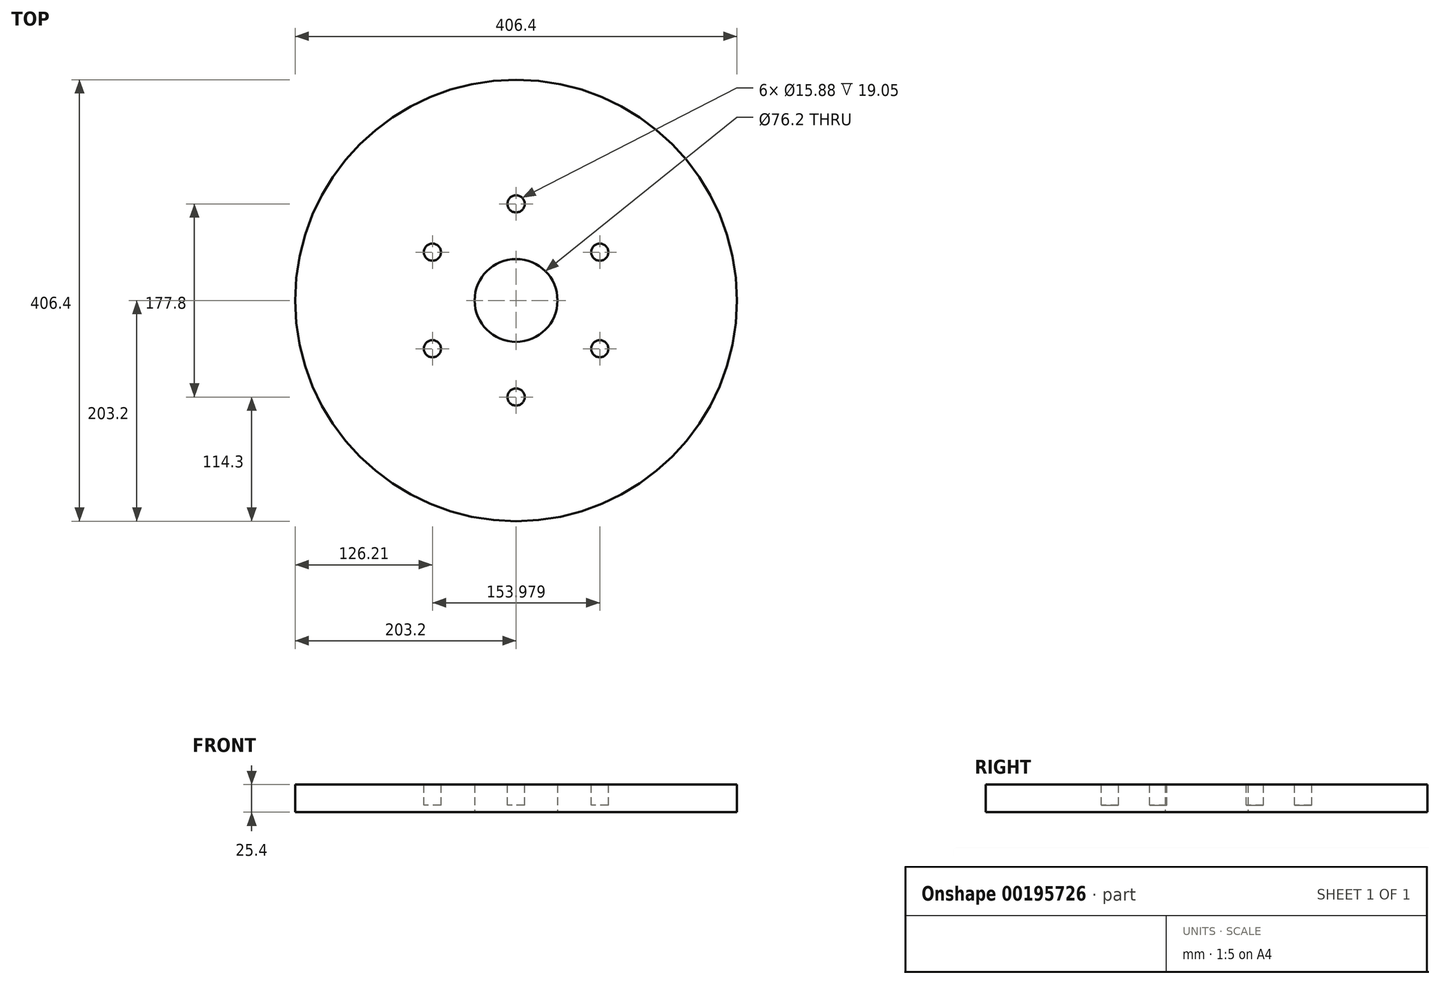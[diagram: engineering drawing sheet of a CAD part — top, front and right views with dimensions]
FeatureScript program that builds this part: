
annotation { "Feature Type Name" : "Feature", "Feature Type Description" : "" }
export const myFeature = defineFeature(function(context is Context, id is Id, definition is map)
    precondition{}
    {
        {
            var Q0;
            Q0=qCreatedBy(makeId("Top.planeOp"),FACE);
            var sketch = newSketch(context, id + "F0", { "sketchPlane" : qUnion([Q0])});
            skCircle(sketch, "E0", {"center": v(0, 0) * mm, "radius": 203.2 * mm});
            skCircle(sketch, "E1", {"center": v(0, 0) * mm, "radius": 38.1 * mm});
            skSolve(sketch);
        }
        {
            var Q0;
            Q0 = qSketchRegion(id + "F0", true);
            extrude(context, id + "F1", {"entities" : qUnion([Q0]), "depth" : 25.4 * mm});
        }
        {
            var Q0;
            Q0=makeQuery(id+"F1.opExtrude","CAP_FACE",FACE,{"disambiguationData":[OSD([sQuery(id+"F0.wireOp",EDGE,"E0"),sQuery(id+"F0.wireOp",EDGE,"E1")])],"isStart":false});
            var sketch = newSketch(context, id + "F2", { "sketchPlane" : qUnion([Q0])});
            skCircle(sketch, "E2", {"center": v(0, 88.9) * mm, "radius": 7.94 * mm});
            skCircle(sketch, "E3.1.0", {"center": v(-76.99, 44.45) * mm, "radius": 7.94 * mm});
            skCircle(sketch, "E3.2.0", {"center": v(-76.99, -44.45) * mm, "radius": 7.94 * mm});
            skCircle(sketch, "E3.3.0", {"center": v(0, -88.9) * mm, "radius": 7.94 * mm});
            skCircle(sketch, "E3.4.0", {"center": v(76.99, -44.45) * mm, "radius": 7.94 * mm});
            skCircle(sketch, "E3.5.0", {"center": v(76.99, 44.45) * mm, "radius": 7.94 * mm});
            skPoint(sketch, "E3.center", {"position": v(0, 0) * mm});
            skLineSegment(sketch, "E4", {"start": v(0, 0) * mm, "end": v(0, 142.6) * mm});
            skLineSegment(sketch, "E5", {"start": v(0, 0) * mm, "end": v(0, 88.9) * mm});
            skSolve(sketch);
        }
        {
            var Q0;
            Q0 = qSketchRegion(id + "F2", true);
            extrude(context, id + "F3", {"entities" : qUnion([Q0]), "operationType" : NewBodyOperationType.REMOVE, "oppositeDirection" : true, "depth" : 19.05 * mm, "offsetDistance" : 25.4 * mm});
        }
    });
